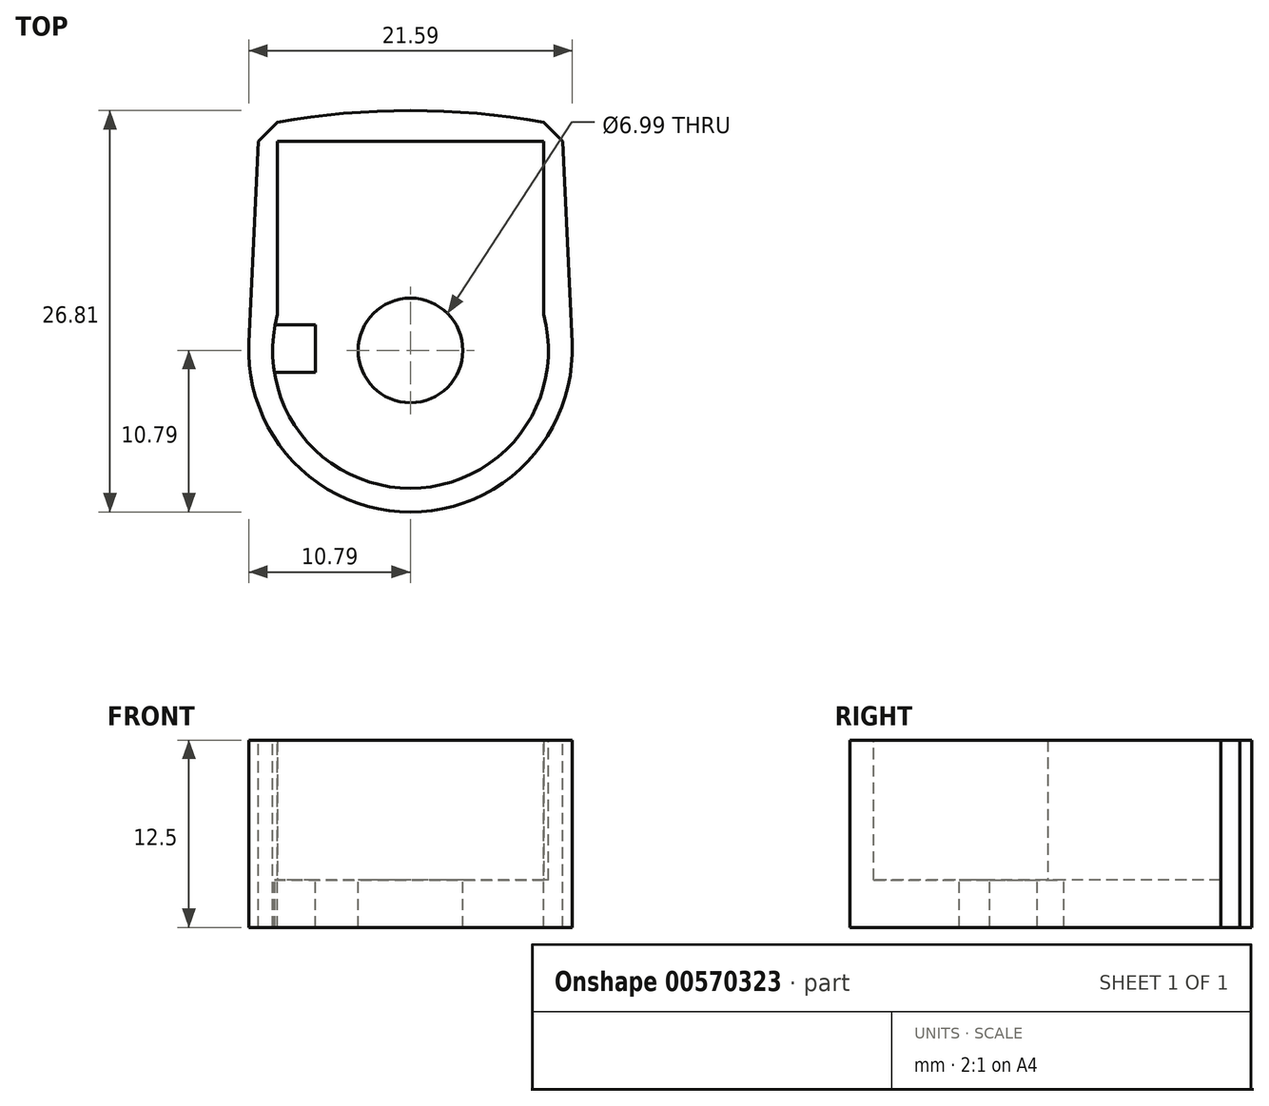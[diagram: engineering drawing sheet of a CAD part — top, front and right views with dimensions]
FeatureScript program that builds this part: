
annotation { "Feature Type Name" : "Feature", "Feature Type Description" : "" }
export const myFeature = defineFeature(function(context is Context, id is Id, definition is map)
    precondition{}
    {
        {
            var Q0;
            Q0=qCreatedBy(makeId("Top.planeOp"),FACE);
            var sketch = newSketch(context, id + "F0", { "sketchPlane" : qUnion([Q0])});
            skCircle(sketch, "E0", {"center": v(0, 0) * mm, "radius": 9.2 * mm});
            skLineSegment(sketch, "E1", {"start": v(0, 0) * mm, "end": v(8.9, 0) * mm});
            skLineSegment(sketch, "E2", {"start": v(8.9, 0) * mm, "end": v(8.9, 13.97) * mm});
            skLineSegment(sketch, "E3", {"start": v(8.9, 13.97) * mm, "end": v(-8.89, 13.97) * mm});
            skLineSegment(sketch, "E4", {"start": v(-8.89, 13.97) * mm, "end": v(-8.89, 0) * mm});
            skLineSegment(sketch, "E5", {"start": v(-8.89, 0) * mm, "end": v(0, 0) * mm});
            skCircle(sketch, "E6", {"center": v(0, 0) * mm, "radius": 10.8 * mm});
            skLineSegment(sketch, "E7", {"start": v(0, 13.97) * mm, "end": v(0, 15.24) * mm});
            skPoint(sketch, "E7.endSnap0", {"position": v(0, 13.97) * mm});
            skLineSegment(sketch, "E8", {"start": v(-8.89, 13.97) * mm, "end": v(-10.16, 13.97) * mm});
            skLineSegment(sketch, "E9", {"start": v(8.9, 13.97) * mm, "end": v(10.16, 13.97) * mm});
            skLineSegment(sketch, "E10", {"start": v(-10.16, 13.97) * mm, "end": v(-10.8, 0) * mm});
            skLineSegment(sketch, "E11", {"start": v(10.16, 13.97) * mm, "end": v(10.8, 0) * mm});
            skCircle(sketch, "E12", {"center": v(0, 0) * mm, "radius": 3.5 * mm});
            skLineSegment(sketch, "E13", {"start": v(0, 0) * mm, "end": v(-6.35, 0) * mm});
            skLineSegment(sketch, "E14", {"start": v(-6.35, 0) * mm, "end": v(-6.35, 1.71) * mm});
            skLineSegment(sketch, "E15", {"start": v(-6.35, 1.71) * mm, "end": v(-6.35, -1.46) * mm});
            skLineSegment(sketch, "E16", {"start": v(-6.35, -1.46) * mm, "end": v(-9.1, -1.46) * mm});
            skLineSegment(sketch, "E17", {"start": v(-6.35, 1.71) * mm, "end": v(-9.05, 1.71) * mm});
            skLineSegment(sketch, "E18", {"start": v(-8.89, 13.97) * mm, "end": v(-8.89, 15.24) * mm});
            skLineSegment(sketch, "E19", {"start": v(8.9, 13.97) * mm, "end": v(8.9, 15.24) * mm});
            skLineSegment(sketch, "E20", {"start": v(8.9, 15.24) * mm, "end": v(10.16, 13.97) * mm});
            skLineSegment(sketch, "E21", {"start": v(-10.16, 13.97) * mm, "end": v(-8.89, 15.24) * mm});
            skArc(sketch, "E22", {"start": v(8.89, 15.24) * mm, "mid": v(0, 16.02) * mm, "end": v(-8.9, 15.24) * mm});
            skSolve(sketch);
        }
        {
            var Q0;
            Q0 = qSketchRegion(id + "F0", true);
            var Q1;
            {var subQ3=sQuery(id+"F0.wireOp",EDGE,"E6");var subQ6=sQuery(id+"F0.wireOp",EDGE,"E2");var subQ8=makeQuery(id+"F0.imprint","INTERSECT",VERTEX,{"derivedFrom":[subQ6,subQ3]});Q1=makeQuery(id+"F0.imprint","IMPRINT",FACE,{"disambiguationData":[TD([[makeQuery(id+"F0.imprint","IMPRINT",EDGE,{"disambiguationData":[TD([[subQ8,-1.0]])],"derivedFrom":subQ3}),-1.0]])]});}
            var Q2;
            {var subQ0=sQuery(id+"F0.wireOp",EDGE,"E4");var subQ1=sQuery(id+"F0.wireOp",EDGE,"E0");var subQ2=makeQuery(id+"F0.imprint","INTERSECT",VERTEX,{"derivedFrom":[subQ1,subQ0]});Q2=makeQuery(id+"F0.imprint","IMPRINT",FACE,{"disambiguationData":[TD([[makeQuery(id+"F0.imprint","IMPRINT",EDGE,{"disambiguationData":[TD([[subQ2,1.0]])],"derivedFrom":subQ1}),-1.0]])]});}
            var Q3;
            {var subQ0=sQuery(id+"F0.wireOp",EDGE,"E4");var subQ1=sQuery(id+"F0.wireOp",EDGE,"E0");var subQ2=makeQuery(id+"F0.imprint","INTERSECT",VERTEX,{"derivedFrom":[subQ1,subQ0]});Q3=makeQuery(id+"F0.imprint","IMPRINT",FACE,{"disambiguationData":[TD([[makeQuery(id+"F0.imprint","IMPRINT",EDGE,{"disambiguationData":[TD([[subQ2,1.0]])],"derivedFrom":subQ1}),1.0]])]});}
            var Q4;
            {var subQ9=sQuery(id+"F0.wireOp",EDGE,"E16");Q4=makeQuery(id+"F0.imprint","IMPRINT",FACE,{"disambiguationData":[TD([[makeQuery(id+"F0.imprint","IMPRINT",EDGE,{"derivedFrom":subQ9}),1.0]])]});}
            var Q5;
            {var subQ0=sQuery(id+"F0.wireOp",EDGE,"E17");var subQ1=sQuery(id+"F0.wireOp",EDGE,"E0");var subQ2=makeQuery(id+"F0.imprint","INTERSECT",VERTEX,{"derivedFrom":[subQ1,subQ0]});Q5=makeQuery(id+"F0.imprint","IMPRINT",FACE,{"disambiguationData":[TD([[makeQuery(id+"F0.imprint","IMPRINT",EDGE,{"disambiguationData":[TD([[subQ2,1.0]])],"derivedFrom":subQ1}),1.0]])]});}
            extrude(context, id + "F1", {"entities" : qUnion([Q0, Q1, Q2, Q3, Q4, Q5]), "oppositeDirection" : true, "depth" : 3.17 * mm, "offsetDistance" : 25.4 * mm});
        }
        {
            var Q0;
            {var subQ0=sQuery(id+"F0.wireOp",EDGE,"E8");Q0=makeQuery(id+"F0.imprint","IMPRINT",FACE,{"disambiguationData":[TD([[makeQuery(id+"F0.imprint","IMPRINT",EDGE,{"derivedFrom":subQ0}),1.0]])]});}
            var Q1;
            {var subQ0=sQuery(id+"F0.wireOp",EDGE,"E0");var subQ9=makeQuery(id+"F0.imprint","INTERSECT",VERTEX,{"derivedFrom":[subQ0,sQuery(id+"F0.wireOp",EDGE,"E17")]});Q1=makeQuery(id+"F0.imprint","IMPRINT",FACE,{"disambiguationData":[TD([[makeQuery(id+"F0.imprint","IMPRINT",EDGE,{"disambiguationData":[TD([[subQ9,1.0]])],"derivedFrom":subQ0}),-1.0]])]});}
            var Q2;
            {var subQ0=sQuery(id+"F0.wireOp",EDGE,"E9");Q2=makeQuery(id+"F0.imprint","IMPRINT",FACE,{"disambiguationData":[TD([[makeQuery(id+"F0.imprint","IMPRINT",EDGE,{"derivedFrom":subQ0}),-1.0]])]});}
            var Q3;
            {var subQ2=sQuery(id+"F0.wireOp",EDGE,"E7");Q3=makeQuery(id+"F0.imprint","IMPRINT",FACE,{"disambiguationData":[TD([[makeQuery(id+"F0.imprint","IMPRINT",EDGE,{"derivedFrom":subQ2}),-1.0]])]});}
            var Q4;
            {var subQ2=sQuery(id+"F0.wireOp",EDGE,"E7");Q4=makeQuery(id+"F0.imprint","IMPRINT",FACE,{"disambiguationData":[TD([[makeQuery(id+"F0.imprint","IMPRINT",EDGE,{"derivedFrom":subQ2}),1.0]])]});}
            var Q5;
            {var subQ0=sQuery(id+"F0.wireOp",EDGE,"E18");Q5=makeQuery(id+"F0.imprint","IMPRINT",FACE,{"disambiguationData":[TD([[makeQuery(id+"F0.imprint","IMPRINT",EDGE,{"derivedFrom":subQ0}),-1.0]])]});}
            var Q6;
            Q6=makeQuery(id+"F0.imprint","IMPRINT",FACE,{"disambiguationData":[TD([[makeQuery(id+"F0.imprint","IMPRINT",EDGE,{"derivedFrom":sQuery(id+"F0.wireOp",EDGE,"E8")}),-1.0]])]});
            var Q7;
            Q7=makeQuery(id+"F0.imprint","IMPRINT",FACE,{"disambiguationData":[TD([[makeQuery(id+"F0.imprint","IMPRINT",EDGE,{"derivedFrom":sQuery(id+"F0.wireOp",EDGE,"E9")}),1.0]])]});
            extrude(context, id + "F2", {"entities" : qUnion([Q0, Q1, Q2, Q3, Q4, Q5, Q6, Q7]), "operationType" : NewBodyOperationType.ADD, "depth" : 9.32 * mm, "offsetDistance" : 25.4 * mm});
        }
    });
